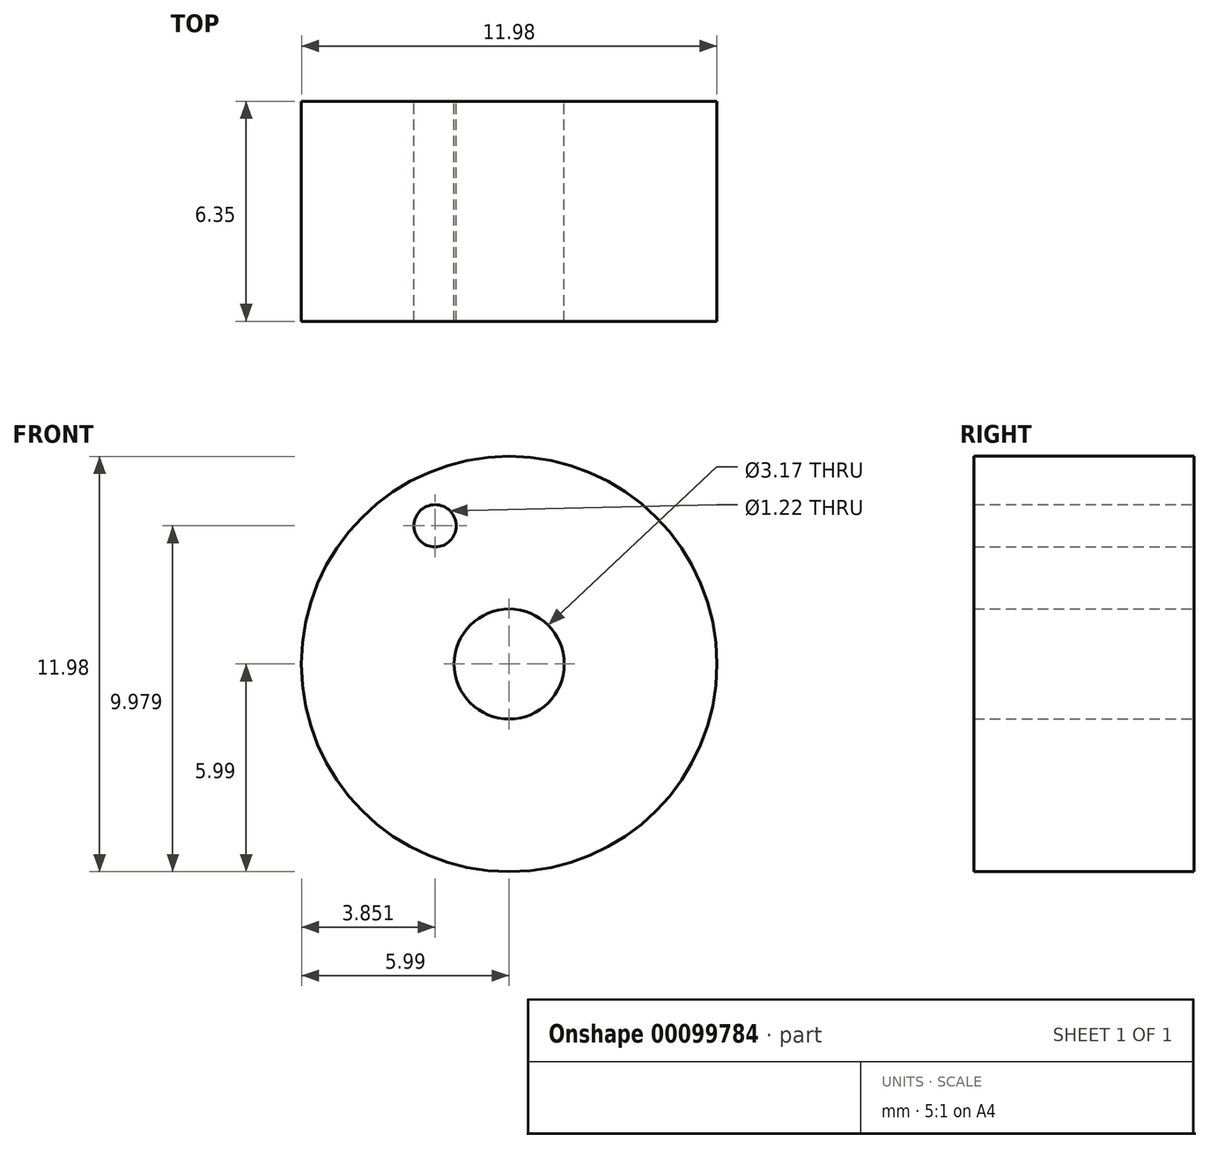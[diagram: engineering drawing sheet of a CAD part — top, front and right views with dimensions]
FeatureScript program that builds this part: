
annotation { "Feature Type Name" : "Feature", "Feature Type Description" : "" }
export const myFeature = defineFeature(function(context is Context, id is Id, definition is map)
    precondition{}
    {
        {
            var Q0;
            Q0=qCreatedBy(makeId("Front.planeOp"),FACE);
            var sketch = newSketch(context, id + "F0", { "sketchPlane" : qUnion([Q0])});
            skCircle(sketch, "E0", {"center": v(0, 0) * mm, "radius": 6 * mm});
            skCircle(sketch, "E1", {"center": v(0, 0) * mm, "radius": 1.59 * mm});
            skCircle(sketch, "E2", {"center": v(-2.14, 3.99) * mm, "radius": 0.6 * mm});
            skSolve(sketch);
        }
        {
            var Q0;
            Q0=makeQuery(id+"F0.imprint","IMPRINT",FACE,{"disambiguationData":[TD([[makeQuery(id+"F0.imprint","IMPRINT",EDGE,{"derivedFrom":sQuery(id+"F0.wireOp",EDGE,"E0")}),1.0]])]});
            extrude(context, id + "F1", {"entities" : qUnion([Q0]), "depth" : 6.35 * mm});
        }
    });
